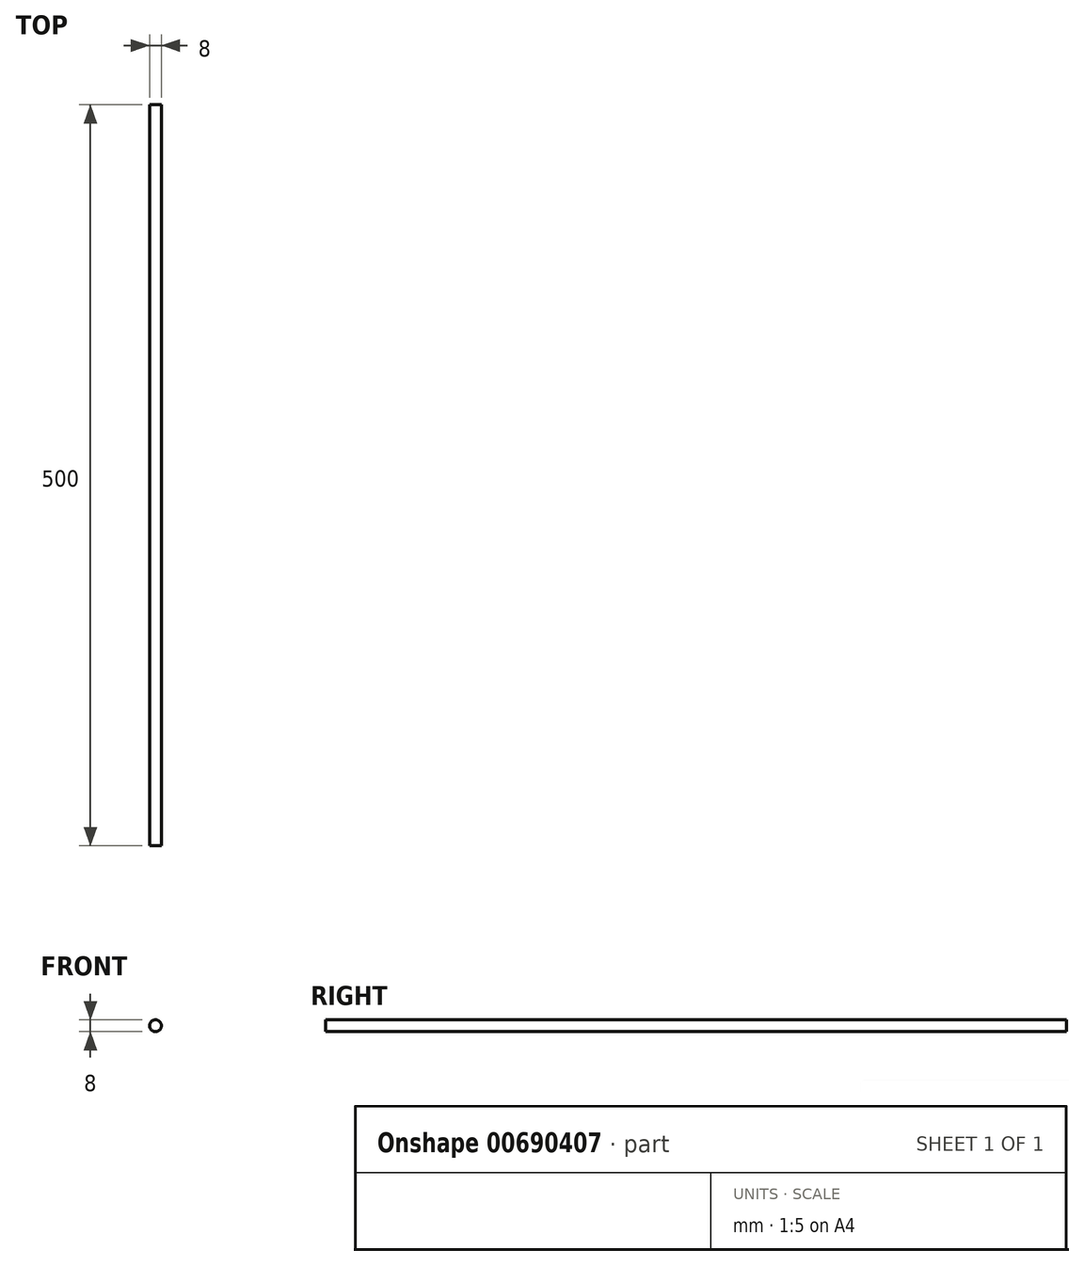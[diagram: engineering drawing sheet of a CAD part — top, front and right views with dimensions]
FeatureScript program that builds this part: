
annotation { "Feature Type Name" : "Feature", "Feature Type Description" : "" }
export const myFeature = defineFeature(function(context is Context, id is Id, definition is map)
    precondition{}
    {
        {
            var Q0;
            Q0=qCreatedBy(makeId("Front.planeOp"),FACE);
            var sketch = newSketch(context, id + "F0", { "sketchPlane" : qUnion([Q0])});
            skCircle(sketch, "E0", {"center": v(0, 0) * mm, "radius": 4 * mm});
            skSolve(sketch);
        }
        {
            var Q0;
            Q0=makeQuery(id+"F0.imprint","IMPRINT",FACE,{"disambiguationData":[TD([[makeQuery(id+"F0.imprint","IMPRINT",EDGE,{"derivedFrom":sQuery(id+"F0.wireOp",EDGE,"E0")}),1.0]])]});
            extrude(context, id + "F1", {"entities" : qUnion([Q0]), "depth" : 500 * mm, "offsetDistance" : 25 * mm});
        }
    });
